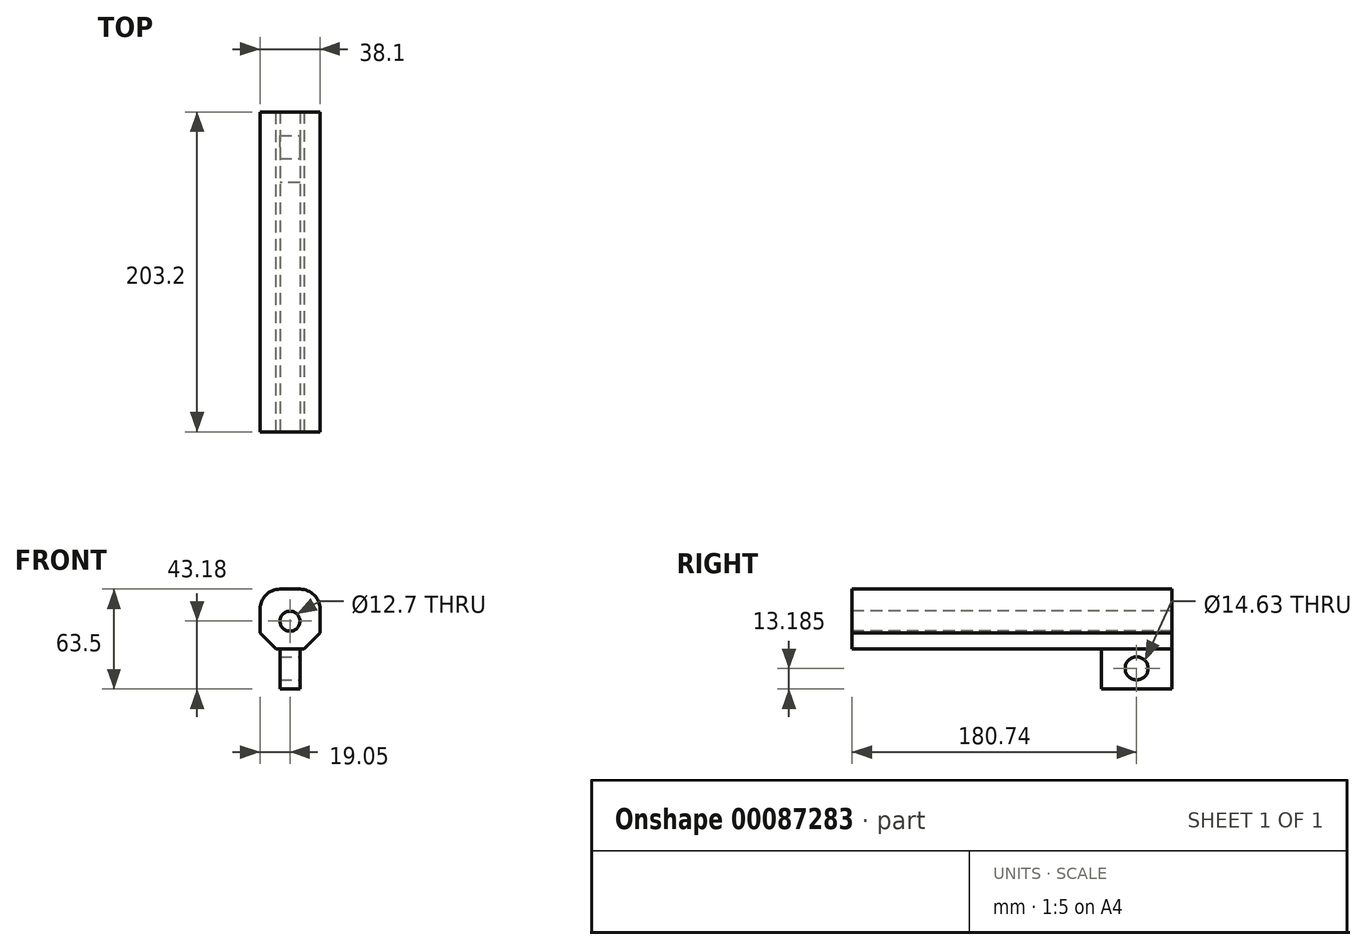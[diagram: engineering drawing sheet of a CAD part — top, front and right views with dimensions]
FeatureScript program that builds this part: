
annotation { "Feature Type Name" : "Feature", "Feature Type Description" : "" }
export const myFeature = defineFeature(function(context is Context, id is Id, definition is map)
    precondition{}
    {
        {
            var Q0;
            Q0=qCreatedBy(makeId("Right.planeOp"),FACE);
            var sketch = newSketch(context, id + "F0", { "sketchPlane" : qUnion([Q0])});
            skLineSegment(sketch, "E0.bottom", {"start": v(22.46, 38.1) * mm, "end": v(-180.74, 38.1) * mm});
            skLineSegment(sketch, "E0.top", {"start": v(22.46, 0) * mm, "end": v(-180.74, 0) * mm});
            skLineSegment(sketch, "E0.left", {"start": v(22.46, 38.1) * mm, "end": v(22.46, 0) * mm});
            skLineSegment(sketch, "E0.right", {"start": v(-180.74, 38.1) * mm, "end": v(-180.74, 0) * mm});
            skLineSegment(sketch, "E1.bottom", {"start": v(-180.74, 25.4) * mm, "end": v(22.46, 25.4) * mm});
            skLineSegment(sketch, "E1.top", {"start": v(-180.74, 12.7) * mm, "end": v(22.46, 12.7) * mm});
            skLineSegment(sketch, "E1.left", {"start": v(-180.74, 25.4) * mm, "end": v(-180.74, 12.7) * mm});
            skLineSegment(sketch, "E1.right", {"start": v(22.46, 25.4) * mm, "end": v(22.46, 12.7) * mm});
            skPoint(sketch, "E1.middle", {"position": v(-79.14, 19.05) * mm});
            skPoint(sketch, "E1.middle.positionSnap0", {"position": v(-79.14, 38.1) * mm});
            skPoint(sketch, "E1.middle.positionSnap1", {"position": v(22.46, 19.05) * mm});
            skPoint(sketch, "E1.centerSnap0", {"position": v(-79.14, 38.1) * mm});
            skPoint(sketch, "E1.centerSnap1", {"position": v(22.46, 19.05) * mm});
            skSolve(sketch);
        }
        {
            var Q0;
            Q0 = qSketchRegion(id + "F0", true);
            extrude(context, id + "F1", {"entities" : qUnion([Q0]), "depth" : 38.1 * mm});
        }
        {
            var Q0;
            Q0=makeQuery(id+"F1.opExtrude","SWEPT_FACE",FACE,{"disambiguationData":[OSD([sQuery(id+"F0.wireOp",EDGE,"E0.top")])]});
            var sketch = newSketch(context, id + "F2", { "sketchPlane" : qUnion([Q0])});
            skLineSegment(sketch, "E2.bottom", {"start": v(25.4, -22.46) * mm, "end": v(12.7, -22.46) * mm});
            skLineSegment(sketch, "E2.top", {"start": v(25.4, 22.46) * mm, "end": v(12.7, 22.46) * mm});
            skLineSegment(sketch, "E2.left", {"start": v(25.4, -22.46) * mm, "end": v(25.4, 22.46) * mm});
            skLineSegment(sketch, "E2.right", {"start": v(12.7, -22.46) * mm, "end": v(12.7, 22.46) * mm});
            skPoint(sketch, "E2.middle", {"position": v(19.05, 0) * mm});
            skPoint(sketch, "E2.middle.positionSnap0", {"position": v(19.05, -22.46) * mm});
            skPoint(sketch, "E2.centerSnap0", {"position": v(19.05, -22.46) * mm});
            skSolve(sketch);
        }
        {
            var Q0;
            Q0 = qSketchRegion(id + "F2", true);
            extrude(context, id + "F3", {"entities" : qUnion([Q0]), "operationType" : NewBodyOperationType.ADD, "depth" : 25.4 * mm});
        }
        {
            var Q0;
            Q0=makeQuery(id+"F1.opExtrude","CAP_EDGE",EDGE,{"disambiguationData":[OSD([sQuery(id+"F0.wireOp",EDGE,"E0.bottom")])],"isStart":false});
            var Q1;
            Q1=makeQuery(id+"F1.opExtrude","CAP_EDGE",EDGE,{"disambiguationData":[OSD([sQuery(id+"F0.wireOp",EDGE,"E0.bottom")])],"isStart":true});
            fillet(context, id + "F4", {"entities" : qUnion([Q0, Q1]), "radius" : 12.7 * mm, "tangentPropagation" : true, "allowEdgeOverflow" : false});
        }
        {
            var Q0;
            Q0=makeQuery(id+"F1.opExtrude","CAP_EDGE",EDGE,{"disambiguationData":[OSD([sQuery(id+"F0.wireOp",EDGE,"E0.top")])],"isStart":false});
            var Q1;
            Q1=makeQuery(id+"F1.opExtrude","CAP_EDGE",EDGE,{"disambiguationData":[OSD([sQuery(id+"F0.wireOp",EDGE,"E0.top")])],"isStart":true});
            chamfer(context, id + "F5", {"entities" : qUnion([Q0, Q1]), "width" : 10.16 * mm, "tangentPropagation" : true});
        }
        {
            var Q0;
            Q0=makeQuery(id+"F1.opExtrude","SWEPT_FACE",FACE,{"disambiguationData":[OSD([sQuery(id+"F0.wireOp",EDGE,"E0.right"),sQuery(id+"F0.wireOp",EDGE,"E1.left")])]});
            var sketch = newSketch(context, id + "F6", { "sketchPlane" : qUnion([Q0])});
            skCircle(sketch, "E3", {"center": v(19.05, 17.78) * mm, "radius": 6.35 * mm});
            skPoint(sketch, "E3.centerSnap0", {"position": v(38.1, 17.78) * mm});
            skPoint(sketch, "E3.centerSnap1", {"position": v(19.05, 38.1) * mm});
            skSolve(sketch);
        }
        {
            var Q0;
            Q0 = qSketchRegion(id + "F6", true);
            extrude(context, id + "F7", {"entities" : qUnion([Q0]), "operationType" : NewBodyOperationType.REMOVE, "oppositeDirection" : true, "depth" : 228.6 * mm});
        }
        {
            var Q0;
            Q0=makeQuery(id+"F3.opExtrude","SWEPT_FACE",FACE,{"disambiguationData":[OSD([sQuery(id+"F2.wireOp",EDGE,"E2.left")])]});
            var sketch = newSketch(context, id + "F8", { "sketchPlane" : qUnion([Q0])});
            skCircle(sketch, "E4", {"center": v(0, -12.22) * mm, "radius": 7.31 * mm});
            skSolve(sketch);
        }
        {
            var Q0;
            Q0 = qSketchRegion(id + "F8", true);
            extrude(context, id + "F9", {"entities" : qUnion([Q0]), "operationType" : NewBodyOperationType.REMOVE, "oppositeDirection" : true, "depth" : 25.4 * mm});
        }
    });
